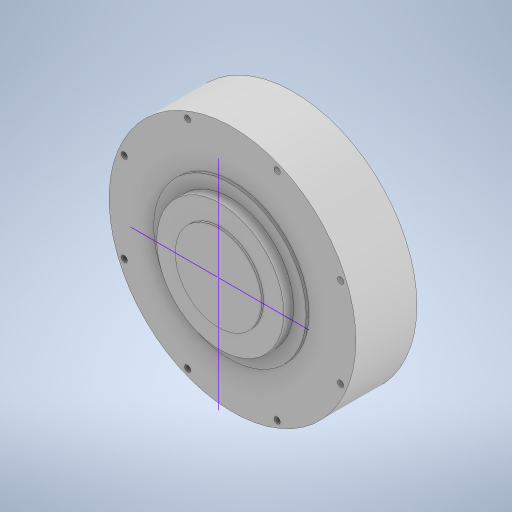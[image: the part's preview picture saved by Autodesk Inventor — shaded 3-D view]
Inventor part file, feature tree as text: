
AUTODESK INVENTOR PART (.ipt)
format: ipt  version: 2023 (Build 270158000, 158)  size: 302,080 bytes
history: native  units: mm
features: sketch x6, extrude x4, other x1, hole x1
ambient origin geometry x8: Origin, YZ Plane, XZ Plane, XY Plane, X Axis, Y Axis, Z Axis, Center Point
bodies: Body1 (feature_tree)
feature tree (12):
  other  "ソリッド1"
  extrude  "押し出し1"  Depth=92.0mm
  hole  "穴1"  [1 undecoded]
  extrude  "押し出し2"  TaperAngle=45.0deg  [1 undecoded]
  extrude  "押し出し3"  TaperAngle=22.5deg  [1 undecoded]
  extrude  "押し出し4"  Depth=40.0mm TaperAngle=360.0deg
  sketch  "スケッチ6"
  sketch  "スケッチ1"
  sketch  "スケッチ2"
  sketch  "スケッチ3"
  sketch  "スケッチ4"
  sketch  "スケッチ5"
note: 3 required parameter values undecoded (feature->parameter linkage not recoverable at this tier; creation-order binding heuristic only, values carry confidence <= 0.55)
